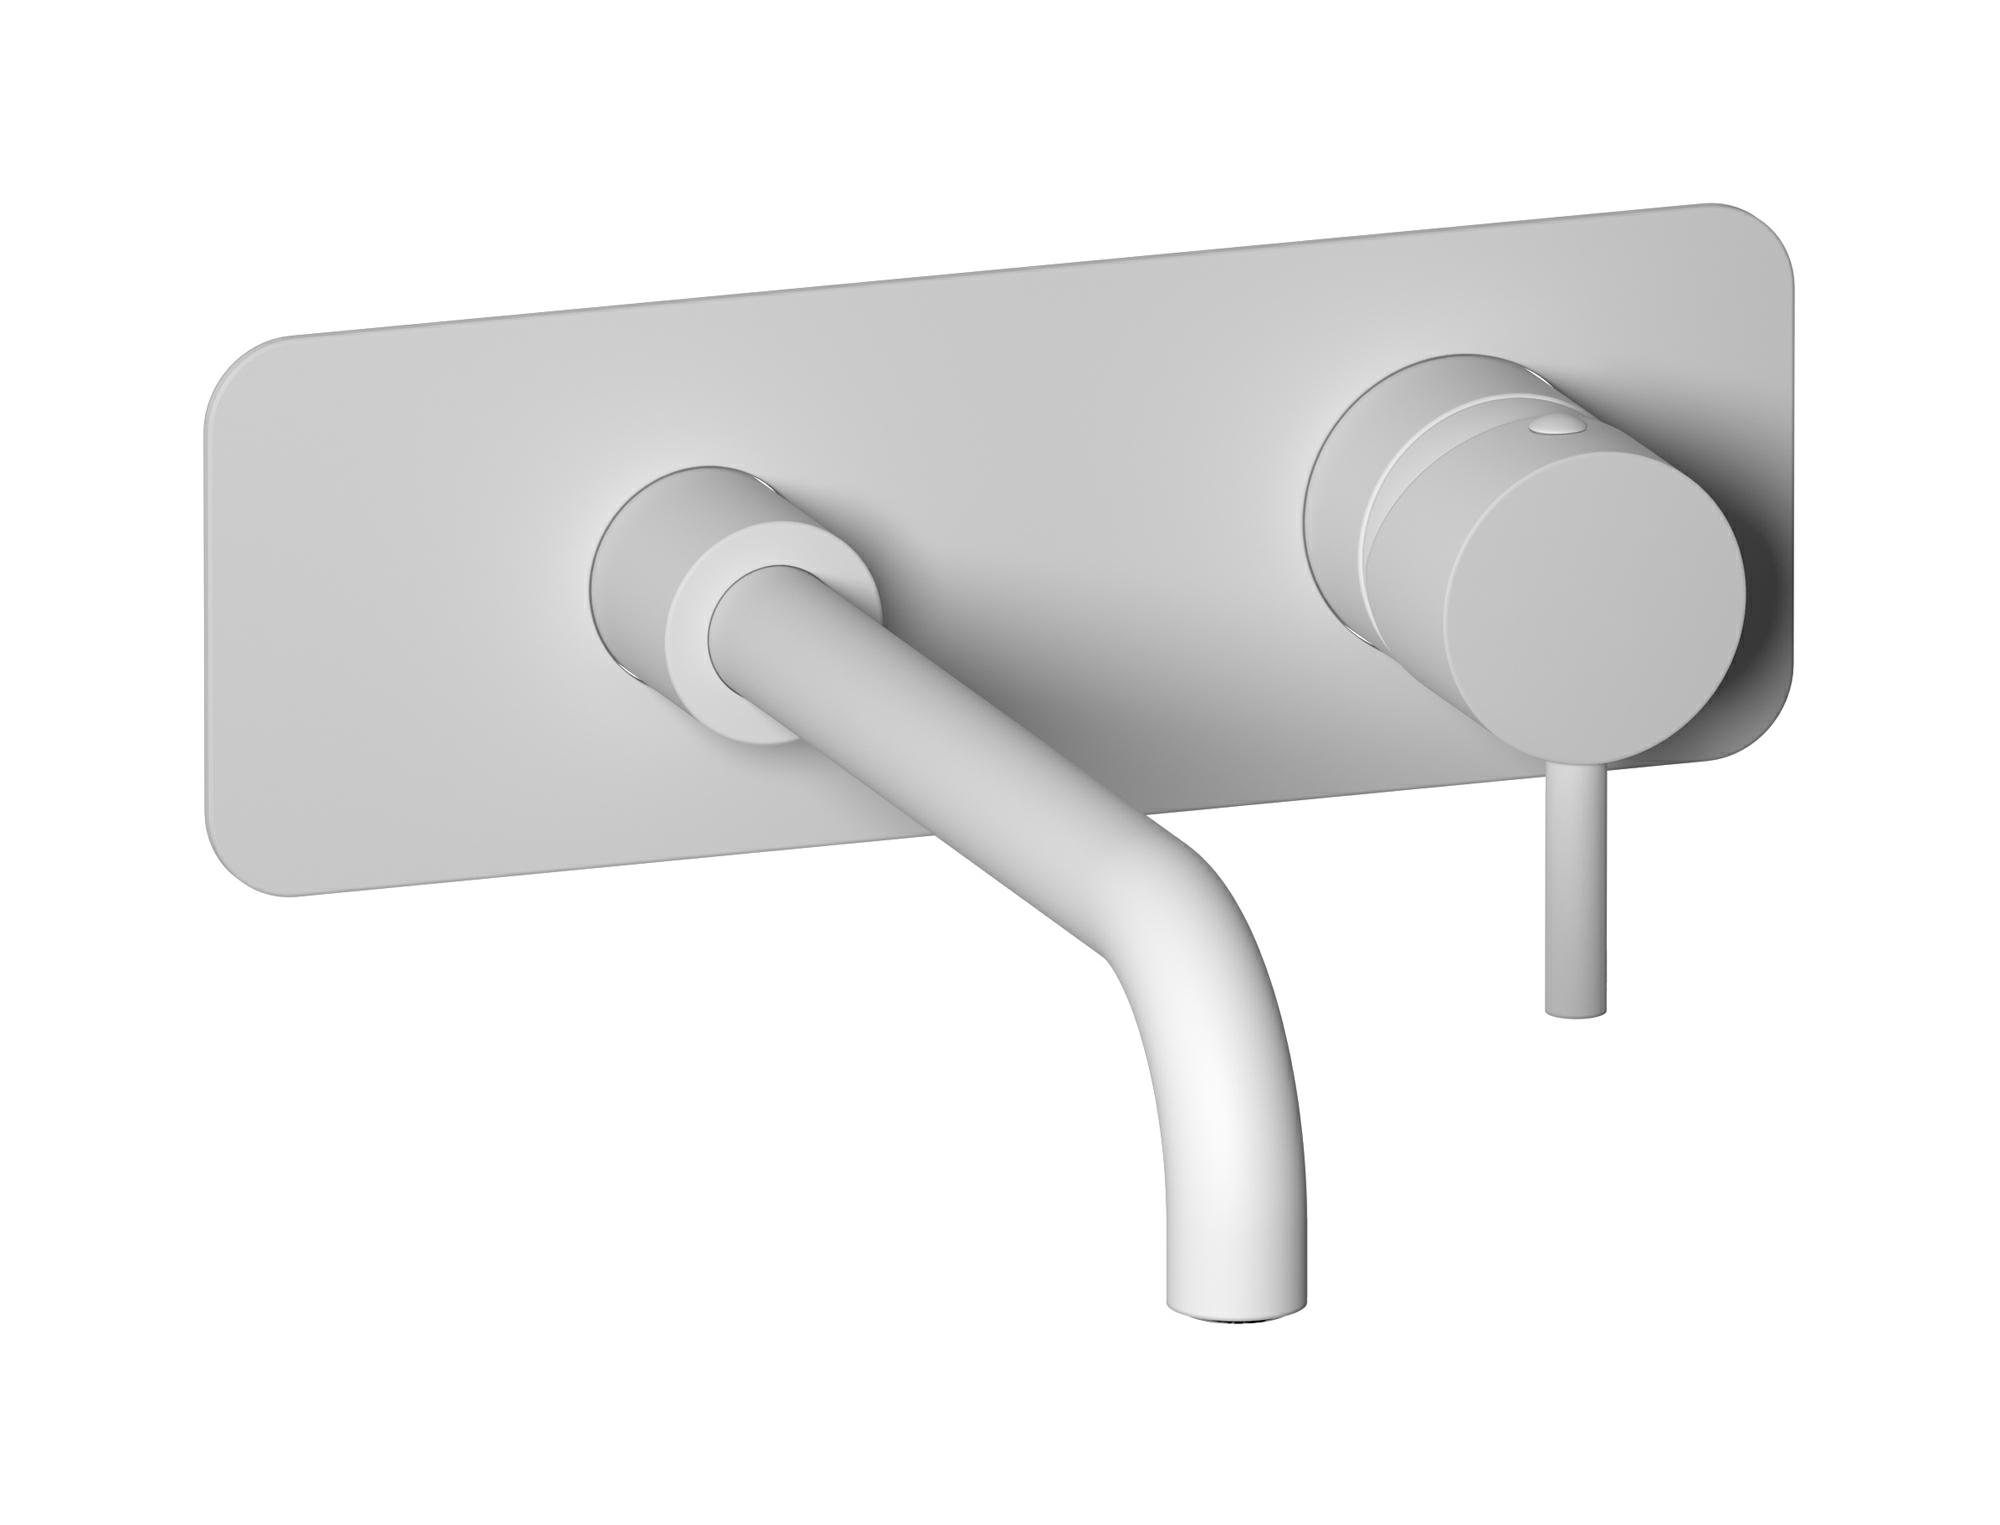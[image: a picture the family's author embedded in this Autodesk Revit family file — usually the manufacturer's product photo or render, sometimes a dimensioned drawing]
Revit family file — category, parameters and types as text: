
# Revit family: MT206
name_source: partatom
category: Apparecchi idraulici
units: mm (PartAtom-declared; Revit-internal decimal feet)

## family parameters
Basato su piano di lavoro = No
Condiviso = No
Mantieni orientamento annotazione = No
Numero OmniClass = 23.45.55.17
Punto di calcolo locali = No
Quota connettore circolare = Usa diametro
Sempre verticale = Sì
Taglio con vuoti quando caricato = No
Tipo di parte = Normale
Titolo OmniClass = Mixing Faucets

## types (13) — shared parameters
Cold water inlet = 10 mm  [stored 0.0328084 ft]
Commenti sul tipo = Washbasin mixer
Connessione CW = No
Connessione HW = No
Connessione di scarico = No
Connessione di ventilazione = No
Descrizione = Wall mounted washbasin mixer complete with drain
Hot water inlet = 10 mm  [stored 0.0328084 ft]
Produttore = IB Rubinetterie S.p.A.
URL = https://www.weareib.it
zero-valued in all types: Prospetto di default

## per-type parameters (varying)
| type | Finishes surface | Immagine tipo | Modello |
| Chrome | IB_Chrome | MT206CC.jpg | MT206CC |
| Brushed nickel | IB_Brushed nickel | MT206SS.jpg | MT206SS |
| Matt white | IB_matt white | MT206BO.jpg | MT206BO |
| Matt black | IB_matt black | MT206NP.jpg | MT206NP |
| Natural brass | IB_Brass | MT206ON.jpg | MT206ON |
| Black chrome | IB_Black chrome | MT206CF.jpg | MT206CF |
| Brushed black chrome | IB_Brushed black chrome | MT206CS.jpg | MT206CS |
| Pale gold | IB_Pale gold | MT206II.jpg | MT206II |
| Brushed pale gold | IB_brushed pale gold | MT206IS.jpg | MT206IS |
| Rose gold | IB_Rose gold | MT206RS.jpg | MT206RS |
| Brushed rose gold | IB_Brushed rose gold | MT206SR.jpg | MT206SR |
| Gold | IB_gold | MT206OO.jpg | MT206OO |
| Brushed gold | IB_brushed gold | MT206OS.jpg | MT206OS |

note: [stored X ft] marks values corroborated as IEEE doubles in the binary element streams (Revit-internal decimal feet)
